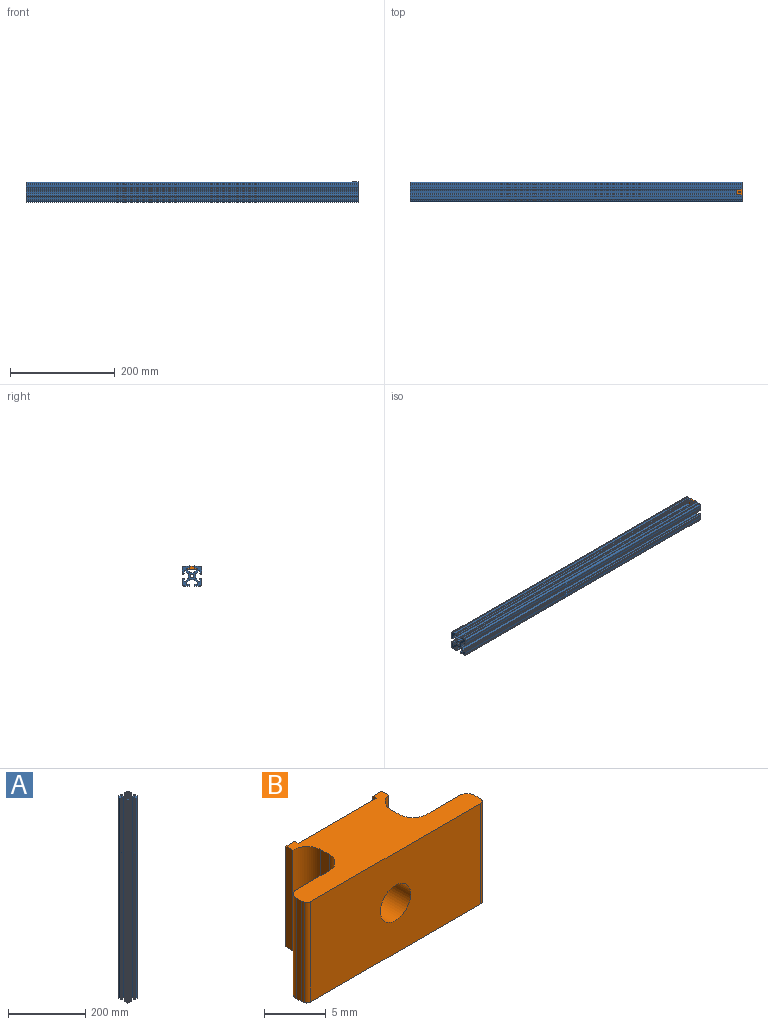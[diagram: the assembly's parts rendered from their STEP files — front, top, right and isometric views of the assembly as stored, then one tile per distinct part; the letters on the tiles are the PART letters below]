
ASSEMBLY  parts=2 mates=1
PART A: 115 faces, bbox 38.1x38.1x634 mm
  f0: cylinder r=4.74mm len=634mm, axis (0,0,-1), area 2359mm2, adj f1,f112,f113,f114
  f1: plane 634x4.77mm, normal (0.71,0.71,0), area 4277.5mm2, adj f0,f2,f113,f114
  f2: cylinder r=0.9mm len=634mm, axis (0,0,-1), area 449mm2, adj f1,f3,f113,f114
  f3: plane 634x0.53mm, normal (1,0,0), area 337.3mm2, adj f2,f4,f113,f114
  f4: cylinder r=0.9mm len=634mm, axis (0,0,-1), area 898mm2, adj f3,f5,f113,f114
  f5: plane 634x3.77mm, normal (0,-1,0), area 2388.7mm2, adj f4,f6,f113,f114
  f6: cylinder r=1.55mm len=634mm, axis (0,0,-1), area 1547.2mm2, adj f5,f7,f113,f114
  f7: plane 634x0.96mm, normal (1,0,0), area 606.6mm2, adj f6,f8,f113,f114
  f8: cylinder r=1.55mm len=634mm, axis (0,0,-1), area 1547.2mm2, adj f7,f9,f113,f114
  f9: plane 634x2.36mm, normal (0,1,0), area 1494.1mm2, adj f8,f10,f113,f114
  f10: cylinder r=0.76mm len=634mm, axis (0,0,-1), area 1517.7mm2, adj f9,f11,f113,f114
  f11: plane 634x4.83mm, normal (0,1,0), area 3061.9mm2, adj f10,f12,f113,f114
  f12: cylinder r=0.76mm len=634mm, axis (0,0,-1), area 1589.8mm2, adj f11,f13,f113,f114
  f13: cylinder r=3.17mm len=634mm, axis (0,0,-1), area 3197mm2, adj f12,f14,f113,f114
  f14: cylinder r=0.76mm len=634mm, axis (0,0,-1), area 1589.8mm2, adj f13,f15,f113,f114
  f15: plane 634x4.83mm, normal (-1,0,0), area 3063.3mm2, adj f14,f16,f113,f114
  f16: cylinder r=0.76mm len=634mm, axis (0,0,-1), area 1589.8mm2, adj f15,f17,f113,f114
  f17: plane 634x2.36mm, normal (-1,0,0), area 1495.4mm2, adj f16,f18,f113,f114
  f18: cylinder r=1.55mm len=634mm, axis (0,0,-1), area 1547.2mm2, adj f17,f19,f113,f114
  f19: plane 634x0.96mm, normal (0,-1,0), area 606.6mm2, adj f18,f20,f113,f114
  f20: cylinder r=1.55mm len=634mm, axis (0,0,-1), area 1547.2mm2, adj f19,f21,f113,f114
  f21: plane 634x3.77mm, normal (1,0,0), area 2388.7mm2, adj f20,f22,f113,f114
  f22: cylinder r=0.9mm len=634mm, axis (0,0,-1), area 898mm2, adj f21,f23,f113,f114
  f23: plane 634x0.57mm, normal (0,-1,0), area 360.3mm2, adj f22,f24,f113,f114
  f24: cylinder r=0.9mm len=634mm, axis (0,0,-1), area 449mm2, adj f23,f25,f113,f114
  f25: plane 634x4.73mm, normal (-0.71,-0.71,0), area 4241.8mm2, adj f24,f26,f113,f114
  f26: cylinder r=4.75mm len=634mm, axis (0,0,-1), area 2365.1mm2, adj f25,f27,f113,f114
  f27: plane 634x3.87mm, normal (-1,0,0), area 2451.6mm2, adj f26,f28,f113,f114
  f28: cylinder r=4.75mm len=634mm, axis (0,0,-1), area 2365.1mm2, adj f27,f29,f113,f114
  f29: plane 634x4.73mm, normal (-0.71,0.71,0), area 4241.8mm2, adj f28,f30,f113,f114
  f30: cylinder r=0.9mm len=634mm, axis (0,0,-1), area 449mm2, adj f29,f31,f113,f114
  f31: plane 634x0.57mm, normal (0,1,0), area 360.3mm2, adj f30,f32,f113,f114
  f32: cylinder r=0.9mm len=634mm, axis (0,0,-1), area 898mm2, adj f31,f33,f113,f114
  f33: plane 634x3.77mm, normal (1,0,0), area 2388.7mm2, adj f32,f34,f113,f114
  f34: cylinder r=1.55mm len=634mm, axis (0,0,-1), area 1547.2mm2, adj f33,f35,f113,f114
  f35: plane 634x0.96mm, normal (0,1,0), area 606.6mm2, adj f34,f36,f113,f114
  f36: cylinder r=1.55mm len=634mm, axis (0,0,-1), area 1547.2mm2, adj f35,f37,f113,f114
  f37: plane 634x2.36mm, normal (-1,0,0), area 1495.4mm2, adj f36,f38,f113,f114
  f38: cylinder r=0.76mm len=634mm, axis (0,0,-1), area 1589.8mm2, adj f37,f39,f113,f114
  f39: plane 634x4.83mm, normal (-1,0,0), area 3063.3mm2, adj f38,f40,f113,f114
  f40: cylinder r=0.76mm len=634mm, axis (0,0,-1), area 1589.8mm2, adj f39,f41,f113,f114
  f41: cylinder r=3.17mm len=634mm, axis (0,0,-1), area 3197mm2, adj f40,f42,f113,f114
  f42: cylinder r=0.76mm len=634mm, axis (0,0,-1), area 1589.8mm2, adj f41,f43,f113,f114
  f43: plane 634x4.83mm, normal (0,-1,0), area 3063.3mm2, adj f42,f44,f113,f114
  f44: cylinder r=0.76mm len=634mm, axis (0,0,-1), area 1589.8mm2, adj f43,f45,f113,f114
  f45: plane 634x2.36mm, normal (0,-1,0), area 1495.4mm2, adj f44,f46,f113,f114
  f46: cylinder r=1.55mm len=634mm, axis (0,0,-1), area 1547.2mm2, adj f45,f47,f113,f114
  f47: plane 634x0.96mm, normal (1,0,0), area 606.6mm2, adj f46,f48,f113,f114
  f48: cylinder r=1.55mm len=634mm, axis (0,0,-1), area 1547.2mm2, adj f47,f49,f113,f114
  f49: plane 634x3.77mm, normal (0,1,0), area 2388.7mm2, adj f48,f50,f113,f114
  f50: cylinder r=0.9mm len=634mm, axis (0,0,-1), area 898mm2, adj f49,f51,f113,f114
  f51: plane 634x0.53mm, normal (1,0,0), area 337.3mm2, adj f50,f52,f113,f114
  f52: cylinder r=0.9mm len=634mm, axis (0,0,-1), area 449mm2, adj f51,f53,f113,f114
  f53: plane 634x4.77mm, normal (0.71,-0.71,0), area 4277.5mm2, adj f52,f54,f113,f114
  f54: cylinder r=4.74mm len=634mm, axis (0,0,-1), area 2359mm2, adj f53,f55,f113,f114
  f55: plane 634x3.8mm, normal (0,-1,0), area 2412mm2, adj f54,f56,f113,f114
  f56: cylinder r=4.74mm len=634mm, axis (0,0,-1), area 2359mm2, adj f55,f57,f113,f114
  f57: plane 634x4.77mm, normal (-0.71,-0.71,0), area 4277.5mm2, adj f56,f58,f113,f114
  f58: cylinder r=0.9mm len=634mm, axis (0,0,-1), area 449mm2, adj f57,f59,f113,f114
  f59: plane 634x0.53mm, normal (-1,0,0), area 337.3mm2, adj f58,f60,f113,f114
  f60: cylinder r=0.9mm len=634mm, axis (0,0,-1), area 898mm2, adj f59,f61,f113,f114
  f61: plane 634x3.77mm, normal (0,1,0), area 2388.7mm2, adj f60,f62,f113,f114
  f62: cylinder r=1.55mm len=634mm, axis (0,0,-1), area 1547.2mm2, adj f61,f63,f113,f114
  f63: plane 634x0.96mm, normal (-1,0,0), area 606.6mm2, adj f62,f64,f113,f114
  f64: cylinder r=1.55mm len=634mm, axis (0,0,-1), area 1547.2mm2, adj f63,f65,f113,f114
  f65: plane 634x2.36mm, normal (0,-1,0), area 1495.4mm2, adj f64,f66,f113,f114
  f66: cylinder r=0.76mm len=634mm, axis (0,0,-1), area 1589.8mm2, adj f65,f67,f113,f114
  f67: plane 634x4.83mm, normal (0,-1,0), area 3063.3mm2, adj f66,f68,f113,f114
  f68: cylinder r=0.76mm len=634mm, axis (0,0,-1), area 1589.8mm2, adj f67,f69,f113,f114
  f69: cylinder r=3.17mm len=634mm, axis (0,0,-1), area 3197mm2, adj f68,f70,f113,f114
  f70: cylinder r=0.76mm len=634mm, axis (0,0,-1), area 1589.8mm2, adj f69,f71,f113,f114
  f71: plane 634x4.83mm, normal (1,0,0), area 3063.3mm2, adj f70,f72,f113,f114
  f72: cylinder r=0.76mm len=634mm, axis (0,0,-1), area 1589.8mm2, adj f71,f73,f113,f114
  f73: plane 634x2.36mm, normal (1,0,0), area 1495.4mm2, adj f72,f74,f113,f114
  f74: cylinder r=1.55mm len=634mm, axis (0,0,-1), area 1547.2mm2, adj f73,f75,f113,f114
  f75: plane 634x0.96mm, normal (0,1,0), area 606.6mm2, adj f74,f76,f113,f114
  f76: cylinder r=1.55mm len=634mm, axis (0,0,-1), area 1547.2mm2, adj f75,f77,f113,f114
  f77: plane 634x3.77mm, normal (-1,0,0), area 2388.7mm2, adj f76,f78,f113,f114
  f78: cylinder r=0.9mm len=634mm, axis (0,0,-1), area 898mm2, adj f77,f79,f113,f114
  f79: plane 634x0.57mm, normal (0,1,0), area 360.3mm2, adj f78,f80,f113,f114
  f80: cylinder r=0.9mm len=634mm, axis (0,0,-1), area 449mm2, adj f79,f81,f113,f114
  f81: plane 634x4.73mm, normal (0.71,0.71,0), area 4241.8mm2, adj f80,f82,f113,f114
  f82: cylinder r=4.75mm len=634mm, axis (0,0,-1), area 2365.1mm2, adj f81,f83,f113,f114
  f83: plane 634x3.87mm, normal (1,0,0), area 2451.6mm2, adj f82,f84,f113,f114
  f84: cylinder r=4.75mm len=634mm, axis (0,0,-1), area 2365.1mm2, adj f83,f85,f113,f114
  f85: plane 634x4.73mm, normal (0.71,-0.71,0), area 4241.8mm2, adj f84,f86,f113,f114
  f86: cylinder r=0.9mm len=634mm, axis (0,0,-1), area 449mm2, adj f85,f87,f113,f114
  f87: plane 634x0.57mm, normal (0,-1,0), area 360.3mm2, adj f86,f88,f113,f114
  f88: cylinder r=0.9mm len=634mm, axis (0,0,-1), area 898mm2, adj f87,f89,f113,f114
  f89: plane 634x3.77mm, normal (-1,0,0), area 2388.7mm2, adj f88,f90,f113,f114
  f90: cylinder r=1.55mm len=634mm, axis (0,0,-1), area 1547.2mm2, adj f89,f91,f113,f114
  f91: plane 634x0.96mm, normal (0,-1,0), area 606.6mm2, adj f90,f92,f113,f114
  f92: cylinder r=1.55mm len=634mm, axis (0,0,-1), area 1547.2mm2, adj f91,f93,f113,f114
  f93: plane 634x2.36mm, normal (1,0,0), area 1495.4mm2, adj f92,f94,f113,f114
  f94: cylinder r=0.76mm len=634mm, axis (0,0,-1), area 1589.8mm2, adj f93,f95,f113,f114
  f95: plane 634x4.83mm, normal (1,0,0), area 3063.3mm2, adj f94,f96,f113,f114
  f96: cylinder r=0.76mm len=634mm, axis (0,0,-1), area 1589.8mm2, adj f95,f97,f113,f114
  f97: cylinder r=3.17mm len=634mm, axis (0,0,-1), area 3197mm2, adj f96,f98,f113,f114
  f98: cylinder r=0.76mm len=634mm, axis (0,0,-1), area 1589.8mm2, adj f97,f99,f113,f114
  f99: plane 634x4.83mm, normal (0,1,0), area 3061.9mm2, adj f98,f100,f113,f114
  f100: cylinder r=0.76mm len=634mm, axis (0,0,-1), area 1517.7mm2, adj f99,f101,f113,f114
  f101: plane 634x2.36mm, normal (0,1,0), area 1494.1mm2, adj f100,f102,f113,f114
  f102: cylinder r=1.55mm len=634mm, axis (0,0,-1), area 1547.2mm2, adj f101,f103,f113,f114
  f103: plane 634x0.96mm, normal (-1,0,0), area 606.6mm2, adj f102,f104,f113,f114
  f104: cylinder r=1.55mm len=634mm, axis (0,0,-1), area 1547.2mm2, adj f103,f105,f113,f114
  f105: plane 634x3.77mm, normal (0,-1,0), area 2388.7mm2, adj f104,f106,f113,f114
  f106: cylinder r=0.9mm len=634mm, axis (0,0,-1), area 898mm2, adj f105,f107,f113,f114
  f107: plane 634x0.53mm, normal (-1,0,0), area 337.3mm2, adj f106,f108,f113,f114
  f108: cylinder r=0.9mm len=634mm, axis (0,0,-1), area 449mm2, adj f107,f109,f113,f114
  f109: plane 634x4.77mm, normal (-0.71,0.71,0), area 4277.5mm2, adj f108,f110,f113,f114
  f110: cylinder r=4.74mm len=634mm, axis (0,0,-1), area 2359mm2, adj f109,f112,f113,f114
  f111: cylinder r=3.33mm len=634mm, axis (0,0,-1), area 13254.8mm2, adj f113,f114
  f112: plane 634x3.8mm, normal (0,1,0), area 2412mm2, adj f0,f110,f113,f114
  f113: plane 38.1x38.1mm, normal (0,0,1), area 744.2mm2, adj f0,f1,f2,f3,f4,f5,f6,f7
  f114: plane 38.1x38.1mm, normal (0,0,-1), area 744.2mm2, adj f0,f1,f2,f3,f4,f5,f6,f7
PART B: 27 faces, bbox 20.5x6.9x10 mm
  f0: plane 10x3.77mm, normal (0,1,0), area 37.7mm2, adj f1,f23,f24,f25
  f1: cylinder r=0.85mm len=10mm, axis (0,0,1), area 13.4mm2, adj f0,f2,f24,f25
  f2: plane 10x0.57mm, normal (-1,0,0), area 5.7mm2, adj f1,f3,f24,f25
  f3: cylinder r=0.85mm len=10mm, axis (0,0,1), area 3mm2, adj f2,f4,f24,f25
  f4: cylinder r=0.45mm len=10mm, axis (0,0,1), area 5.5mm2, adj f3,f5,f24,f25
  f5: plane 19.53x10mm, normal (0,-1,0), area 185.6mm2, adj f4,f6,f24,f25,f26
  f6: cylinder r=0.45mm len=10mm, axis (0,0,1), area 5.5mm2, adj f5,f7,f24,f25
  f7: cylinder r=0.85mm len=10mm, axis (0,0,1), area 3mm2, adj f6,f8,f24,f25
  f8: plane 10x0.57mm, normal (1,0,0), area 5.7mm2, adj f7,f9,f24,f25
  f9: cylinder r=0.85mm len=10mm, axis (0,0,1), area 13.4mm2, adj f8,f10,f24,f25
  f10: plane 10x3.77mm, normal (0,1,0), area 37.7mm2, adj f9,f11,f24,f25
  f11: cylinder r=1.6mm len=10mm, axis (0,0,1), area 25.2mm2, adj f10,f12,f24,f25
  f12: plane 10x0.96mm, normal (1,0,0), area 9.6mm2, adj f11,f13,f24,f25
  f13: cylinder r=1.54mm len=10mm, axis (0,0,1), area 21.9mm2, adj f12,f14,f24,f25
  f14: plane 10x0.83mm, normal (1,0,0), area 8.3mm2, adj f13,f15,f24,f25
  f15: plane 10x1mm, normal (0,1,0), area 10mm2, adj f14,f16,f24,f25
  f16: plane 10x0.4mm, normal (-1,0,0), area 4mm2, adj f15,f17,f24,f25
  f17: plane 10x9.01mm, normal (0,1,0), area 80.5mm2, adj f16,f18,f24,f25,f26
  f18: plane 10x0.4mm, normal (1,0,0), area 4mm2, adj f17,f19,f24,f25
  f19: plane 10x1mm, normal (0,1,0), area 10mm2, adj f18,f20,f24,f25
  f20: plane 10x0.8mm, normal (-1,0,0), area 8mm2, adj f19,f21,f24,f25
  f21: cylinder r=1.56mm len=10mm, axis (0,0,1), area 25.6mm2, adj f20,f22,f24,f25
  f22: plane 10x0.96mm, normal (-1,0,0), area 9.6mm2, adj f21,f23,f24,f25
  f23: cylinder r=1.6mm len=10mm, axis (0,0,1), area 25.2mm2, adj f0,f22,f24,f25
  f24: plane 20.47x6.92mm, normal (0,0,-1), area 81.1mm2, adj f0,f1,f2,f3,f4,f5,f6,f7
  f25: plane 20.47x6.92mm, normal (0,0,1), area 81.1mm2, adj f0,f1,f2,f3,f4,f5,f6,f7
  f26: cylinder r=1.75mm len=6.52mm, axis (0,-1,0), area 71.7mm2, adj f5,f17
PLACE A rot(axis=(0,-1,0),90deg) t=(473.52,82.15,-112.25)mm
PLACE B rot(axis=(0.58,0.58,0.58),120deg) t=(473.52,82.15,-89.72)mm
MATE planar B.f25 <-> A.f111  axis (1,0,0) through (473.52,82.13,-96.64)mm
